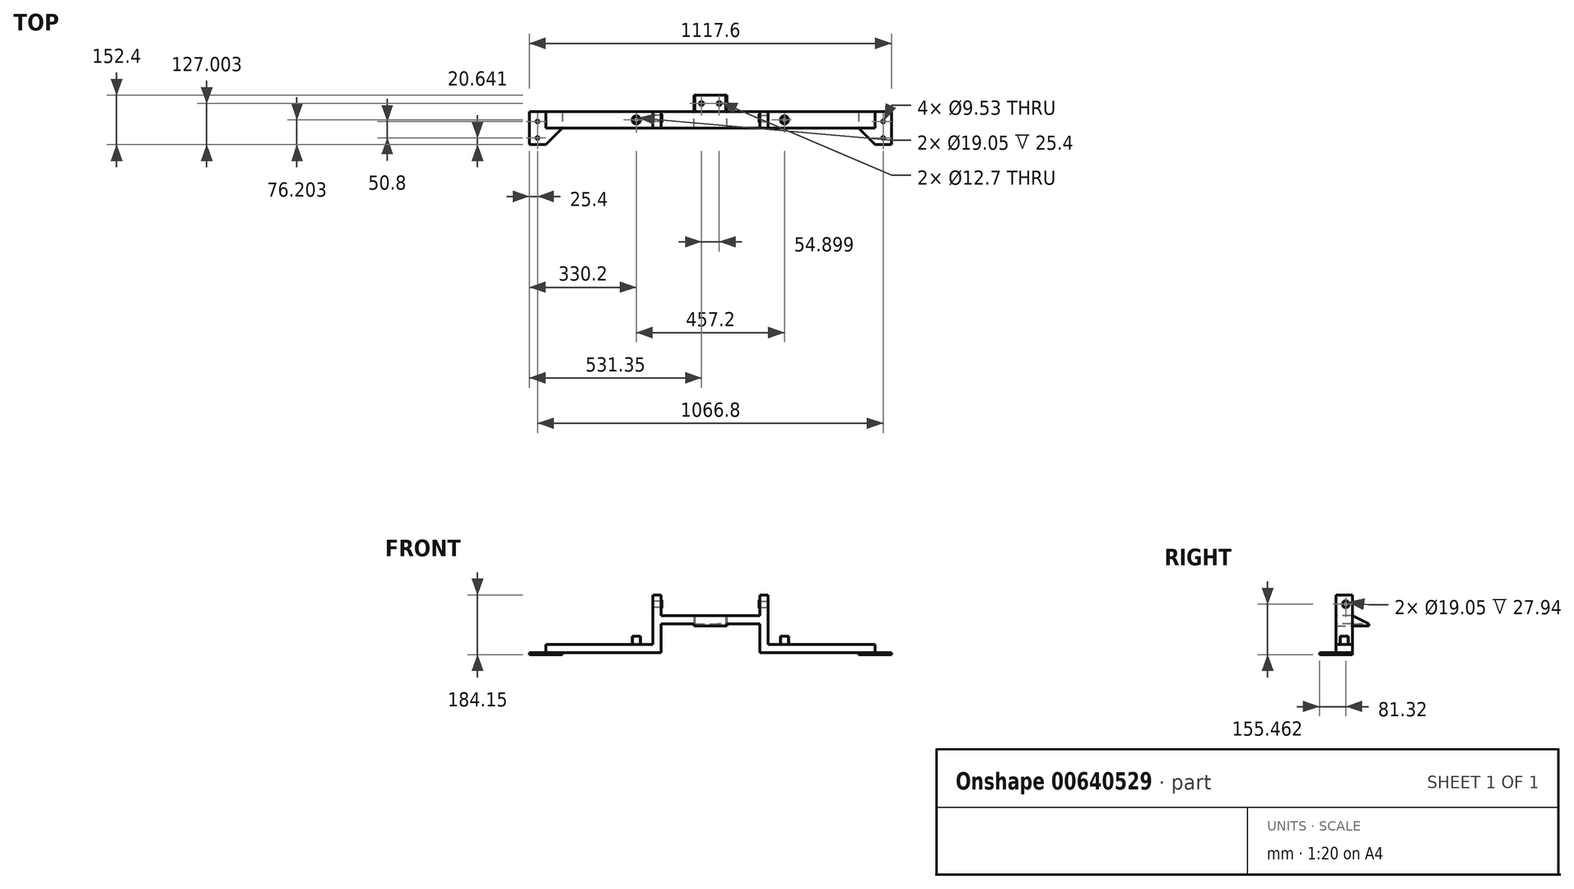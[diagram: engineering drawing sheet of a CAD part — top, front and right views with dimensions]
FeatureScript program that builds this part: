
annotation { "Feature Type Name" : "Feature", "Feature Type Description" : "" }
export const myFeature = defineFeature(function(context is Context, id is Id, definition is map)
    precondition{}
    {
        {
            var Q0;
            Q0=qCreatedBy(makeId("Top.planeOp"),FACE);
            var sketch = newSketch(context, id + "F0", { "sketchPlane" : qUnion([Q0])});
            skLineSegment(sketch, "E0.bottom", {"start": v(0, 37.2) * mm, "end": v(355.6, 37.2) * mm});
            skLineSegment(sketch, "E0.top", {"start": v(0, -13.6) * mm, "end": v(355.6, -13.6) * mm});
            skLineSegment(sketch, "E0.left", {"start": v(0, 37.2) * mm, "end": v(0, -13.6) * mm});
            skLineSegment(sketch, "E0.right", {"start": v(355.6, 37.2) * mm, "end": v(355.6, -13.6) * mm});
            skSolve(sketch);
        }
        {
            var Q0;
            Q0=makeQuery(id+"F0.imprint","IMPRINT",FACE,{"disambiguationData":[TD([[makeQuery(id+"F0.imprint","IMPRINT",EDGE,{"derivedFrom":sQuery(id+"F0.wireOp",EDGE,"E0.bottom")}),-1.0]])]});
            extrude(context, id + "F1", {"entities" : qUnion([Q0]), "depth" : 25.4 * mm, "offsetDistance" : 25.4 * mm});
        }
        {
            var Q0;
            Q0=qCreatedBy(makeId("Top.planeOp"),FACE);
            var sketch = newSketch(context, id + "F2", { "sketchPlane" : qUnion([Q0])});
            skLineSegment(sketch, "E1.0", {"start": v(0, 37.2) * mm, "end": v(355.6, 37.2) * mm});
            skLineSegment(sketch, "E2.0", {"start": v(0, -13.6) * mm, "end": v(355.6, -13.6) * mm});
            skLineSegment(sketch, "E3", {"start": v(304.8, -13.6) * mm, "end": v(355.6, -64.4) * mm});
            skLineSegment(sketch, "E4", {"start": v(355.6, -64.4) * mm, "end": v(406.4, -64.4) * mm});
            skLineSegment(sketch, "E5", {"start": v(406.4, -64.4) * mm, "end": v(406.4, 37.2) * mm});
            skLineSegment(sketch, "E6", {"start": v(406.4, 37.2) * mm, "end": v(304.8, 37.2) * mm});
            skLineSegment(sketch, "E7", {"start": v(304.8, 37.2) * mm, "end": v(304.8, -13.6) * mm});
            skSolve(sketch);
        }
        {
            var Q0;
            Q0 = qSketchRegion(id + "F2", true);
            extrude(context, id + "F3", {"entities" : qUnion([Q0]), "operationType" : NewBodyOperationType.ADD, "oppositeDirection" : true, "depth" : 6.35 * mm, "offsetDistance" : 25.4 * mm});
        }
        {
            var Q0;
            Q0=makeQuery(id+"F3.opExtrude","CAP_FACE",FACE,{"disambiguationData":[OSD([sQuery(id+"F2.wireOp",EDGE,"E3"),sQuery(id+"F2.wireOp",EDGE,"E4"),sQuery(id+"F2.wireOp",EDGE,"E5"),sQuery(id+"F2.wireOp",EDGE,"E6"),sQuery(id+"F2.wireOp",EDGE,"E7")])],"isStart":true});
            var sketch = newSketch(context, id + "F4", { "sketchPlane" : qUnion([Q0])});
            skCircle(sketch, "E8", {"center": v(381, -43.77) * mm, "radius": 4.76 * mm});
            skCircle(sketch, "E9", {"center": v(381, 7.03) * mm, "radius": 4.76 * mm});
            skSolve(sketch);
        }
        {
            var Q0;
            Q0 = qSketchRegion(id + "F4", true);
            extrude(context, id + "F5", {"entities" : qUnion([Q0]), "operationType" : NewBodyOperationType.REMOVE, "oppositeDirection" : true, "depth" : 25.4 * mm, "offsetDistance" : 25.4 * mm});
        }
        {
            var Q0;
            Q0=makeQuery(id+"F1.opExtrude","CAP_FACE",FACE,{"disambiguationData":[OSD([sQuery(id+"F0.wireOp",EDGE,"E0.bottom"),sQuery(id+"F0.wireOp",EDGE,"E0.top"),sQuery(id+"F0.wireOp",EDGE,"E0.left"),sQuery(id+"F0.wireOp",EDGE,"E0.right")])],"isStart":false});
            var sketch = newSketch(context, id + "F6", { "sketchPlane" : qUnion([Q0])});
            skCircle(sketch, "E10", {"center": v(76.2, 11.8) * mm, "radius": 12.7 * mm});
            skCircle(sketch, "E11", {"center": v(76.2, 11.8) * mm, "radius": 9.53 * mm});
            skSolve(sketch);
        }
        {
            var Q0;
            Q0=makeQuery(id+"F6.imprint","IMPRINT",FACE,{"disambiguationData":[TD([[makeQuery(id+"F6.imprint","IMPRINT",EDGE,{"derivedFrom":sQuery(id+"F6.wireOp",EDGE,"E10")}),1.0]])]});
            var Q1;
            Q1=sQuery(id+"F6.wireOp",EDGE,"E10");
            var Q2;
            Q2=sQuery(id+"F6.wireOp",EDGE,"E11");
            extrude(context, id + "F7", {"entities" : qUnion([Q0]), "operationType" : NewBodyOperationType.ADD, "surfaceEntities" : qUnion([Q1, Q2]), "depth" : 25.4 * mm, "offsetDistance" : 25.4 * mm});
        }
        {
            var Q0;
            Q0=makeQuery(id+"F1.opExtrude","CAP_FACE",FACE,{"disambiguationData":[OSD([sQuery(id+"F0.wireOp",EDGE,"E0.bottom"),sQuery(id+"F0.wireOp",EDGE,"E0.top"),sQuery(id+"F0.wireOp",EDGE,"E0.left"),sQuery(id+"F0.wireOp",EDGE,"E0.right")])],"isStart":false});
            var sketch = newSketch(context, id + "F8", { "sketchPlane" : qUnion([Q0])});
            skLineSegment(sketch, "E12.bottom", {"start": v(0, 37.2) * mm, "end": v(25.4, 37.2) * mm});
            skLineSegment(sketch, "E12.top", {"start": v(0, -13.6) * mm, "end": v(25.4, -13.6) * mm});
            skLineSegment(sketch, "E12.left", {"start": v(0, 37.2) * mm, "end": v(0, -13.6) * mm});
            skLineSegment(sketch, "E12.right", {"start": v(25.4, 37.2) * mm, "end": v(25.4, -13.6) * mm});
            skSolve(sketch);
        }
        {
            var Q0;
            Q0 = qSketchRegion(id + "F8", true);
            extrude(context, id + "F9", {"entities" : qUnion([Q0]), "operationType" : NewBodyOperationType.ADD, "depth" : 152.4 * mm, "offsetDistance" : 25.4 * mm});
        }
        {
            var Q0;
            Q0=makeQuery(id+"F9.boolean.opBoolean","MERGE",FACE,{"derivedFrom":[makeQuery(id+"F1.opExtrude","SWEPT_FACE",FACE,{"disambiguationData":[OSD([sQuery(id+"F0.wireOp",EDGE,"E0.left")])]}),makeQuery(id+"F9.opExtrude","SWEPT_FACE",FACE,{"disambiguationData":[OSD([sQuery(id+"F8.wireOp",EDGE,"E12.left")])]})]});
            var sketch = newSketch(context, id + "F10", { "sketchPlane" : qUnion([Q0])});
            skLineSegment(sketch, "E13.bottom", {"start": v(-37.2, 114.3) * mm, "end": v(13.6, 114.3) * mm});
            skLineSegment(sketch, "E13.top", {"start": v(-37.2, 88.9) * mm, "end": v(13.6, 88.9) * mm});
            skLineSegment(sketch, "E13.left", {"start": v(-37.2, 114.3) * mm, "end": v(-37.2, 88.9) * mm});
            skLineSegment(sketch, "E13.right", {"start": v(13.6, 114.3) * mm, "end": v(13.6, 88.9) * mm});
            skSolve(sketch);
        }
        {
            var Q0;
            Q0 = qSketchRegion(id + "F10", true);
            extrude(context, id + "F11", {"entities" : qUnion([Q0]), "operationType" : NewBodyOperationType.ADD, "depth" : 152.4 * mm, "offsetDistance" : 25.4 * mm});
        }
        {
            var Q0;
            {var subQ1=sQuery(id+"F8.wireOp",EDGE,"E12.left");Q0=makeQuery(id+"F11.boolean.opBoolean","SPLIT",FACE,{"disambiguationData":[TD([makeQuery(id+"F11.opExtrude","SWEPT_FACE",FACE,{"disambiguationData":[OSD([sQuery(id+"F10.wireOp",EDGE,"E13.bottom")])]})])],"derivedFrom":makeQuery(id+"F9.boolean.opBoolean","MERGE",FACE,{"derivedFrom":[makeQuery(id+"F1.opExtrude","SWEPT_FACE",FACE,{"disambiguationData":[OSD([sQuery(id+"F0.wireOp",EDGE,"E0.left")])]}),makeQuery(id+"F9.opExtrude","SWEPT_FACE",FACE,{"disambiguationData":[OSD([subQ1])]})]})});}
            var sketch = newSketch(context, id + "F12", { "sketchPlane" : qUnion([Q0])});
            skCircle(sketch, "E14", {"center": v(-16.9, 149.11) * mm, "radius": 12.7 * mm});
            skCircle(sketch, "E15", {"center": v(-16.9, 149.11) * mm, "radius": 9.53 * mm});
            skSolve(sketch);
        }
        {
            var Q0;
            Q0 = qSketchRegion(id + "F12", true);
            extrude(context, id + "F13", {"entities" : qUnion([Q0]), "operationType" : NewBodyOperationType.ADD, "depth" : 2.54 * mm, "offsetDistance" : 25.4 * mm});
        }
        {
            var Q0;
            {var subQ1=sQuery(id+"F8.wireOp",EDGE,"E12.left");Q0=makeQuery(id+"F13.boolean.opBoolean","SPLIT",FACE,{"disambiguationData":[TD([makeQuery(id+"F13.opExtrude","SWEPT_FACE",FACE,{"disambiguationData":[OSD([sQuery(id+"F12.wireOp",EDGE,"E15")])]})])],"derivedFrom":makeQuery(id+"F11.boolean.opBoolean","SPLIT",FACE,{"disambiguationData":[TD([makeQuery(id+"F11.opExtrude","SWEPT_FACE",FACE,{"disambiguationData":[OSD([sQuery(id+"F10.wireOp",EDGE,"E13.bottom")])]})])],"derivedFrom":makeQuery(id+"F9.boolean.opBoolean","MERGE",FACE,{"derivedFrom":[makeQuery(id+"F1.opExtrude","SWEPT_FACE",FACE,{"disambiguationData":[OSD([sQuery(id+"F0.wireOp",EDGE,"E0.left")])]}),makeQuery(id+"F9.opExtrude","SWEPT_FACE",FACE,{"disambiguationData":[OSD([subQ1])]})]})})});}
            var sketch = newSketch(context, id + "F14", { "sketchPlane" : qUnion([Q0])});
            skCircle(sketch, "E16", {"center": v(-16.9, 149.11) * mm, "radius": 9.53 * mm});
            skSolve(sketch);
        }
        {
            var Q0;
            Q0 = qSketchRegion(id + "F14", true);
            extrude(context, id + "F15", {"entities" : qUnion([Q0]), "operationType" : NewBodyOperationType.REMOVE, "oppositeDirection" : true, "depth" : 25.4 * mm, "offsetDistance" : 25.4 * mm});
        }
        {
            var Q0;
            Q0=makeQuery(id+"F11.opExtrude","SWEPT_FACE",FACE,{"disambiguationData":[OSD([sQuery(id+"F10.wireOp",EDGE,"E13.top")])]});
            var sketch = newSketch(context, id + "F16", { "sketchPlane" : qUnion([Q0])});
            skLineSegment(sketch, "E17.bottom", {"start": v(-101.6, 13.6) * mm, "end": v(-152.4, 13.6) * mm});
            skLineSegment(sketch, "E17.top", {"start": v(-101.6, -88) * mm, "end": v(-152.4, -88) * mm});
            skLineSegment(sketch, "E17.left", {"start": v(-101.6, 13.6) * mm, "end": v(-101.6, -88) * mm});
            skLineSegment(sketch, "E17.right", {"start": v(-152.4, 13.6) * mm, "end": v(-152.4, -88) * mm});
            skSolve(sketch);
        }
        {
            var Q0;
            Q0 = qSketchRegion(id + "F16", true);
            extrude(context, id + "F17", {"entities" : qUnion([Q0]), "operationType" : NewBodyOperationType.ADD, "depth" : 6.35 * mm, "offsetDistance" : 25.4 * mm});
        }
        {
            var Q0;
            Q0=makeQuery(id+"F17.opExtrude","CAP_FACE",FACE,{"disambiguationData":[OSD([sQuery(id+"F16.wireOp",EDGE,"E17.bottom"),sQuery(id+"F16.wireOp",EDGE,"E17.top"),sQuery(id+"F16.wireOp",EDGE,"E17.left"),sQuery(id+"F16.wireOp",EDGE,"E17.right")])],"isStart":true});
            var sketch = newSketch(context, id + "F18", { "sketchPlane" : qUnion([Q0])});
            skCircle(sketch, "E18", {"center": v(-124.95, 62.6) * mm, "radius": 6.35 * mm});
            skPoint(sketch, "E18.centerSnap0", {"position": v(-101.6, 62.6) * mm});
            skSolve(sketch);
        }
        {
            var Q0;
            Q0 = qSketchRegion(id + "F18", true);
            extrude(context, id + "F19", {"entities" : qUnion([Q0]), "operationType" : NewBodyOperationType.REMOVE, "oppositeDirection" : true, "depth" : 25.4 * mm, "offsetDistance" : 25.4 * mm});
        }
        {
            var Q0;
            Q0=makeQuery(id+"F17.opExtrude","SWEPT_FACE",FACE,{"disambiguationData":[OSD([sQuery(id+"F16.wireOp",EDGE,"E17.left")])]});
            var sketch = newSketch(context, id + "F20", { "sketchPlane" : qUnion([Q0])});
            skLineSegment(sketch, "E19", {"start": v(88, 88.9) * mm, "end": v(37.2, 114.3) * mm});
            skLineSegment(sketch, "E20", {"start": v(37.2, 114.3) * mm, "end": v(37.2, 82.55) * mm});
            skLineSegment(sketch, "E21", {"start": v(37.2, 82.55) * mm, "end": v(88, 82.55) * mm});
            skLineSegment(sketch, "E22", {"start": v(88, 82.55) * mm, "end": v(37.2, 82.55) * mm});
            skSolve(sketch);
        }
        {
            var Q0;
            {var subQ0=sQuery(id+"F20.wireOp",EDGE,"E19");Q0=makeQuery(id+"F20.imprint","IMPRINT",FACE,{"disambiguationData":[TD([[makeQuery(id+"F20.imprint","IMPRINT",EDGE,{"derivedFrom":subQ0}),1.0]])]});}
            var Q1;
            {var subQ6=sQuery(id+"F20.wireOp",EDGE,"E22");Q1=makeQuery(id+"F20.imprint","IMPRINT",FACE,{"disambiguationData":[TD([[makeQuery(id+"F20.imprint","IMPRINT",EDGE,{"derivedFrom":subQ6}),1.0]])]});}
            extrude(context, id + "F21", {"entities" : qUnion([Q0, Q1]), "operationType" : NewBodyOperationType.ADD, "oppositeDirection" : true, "depth" : 3.17 * mm, "offsetDistance" : 25.4 * mm});
        }
        {
            var Q0;
            Q0=makeQuery(id+"F1.opExtrude","SWEPT_BODY",BODY,{"disambiguationData":[OSD([sQuery(id+"F0.wireOp",EDGE,"E0.bottom"),sQuery(id+"F0.wireOp",EDGE,"E0.top"),sQuery(id+"F0.wireOp",EDGE,"E0.left"),sQuery(id+"F0.wireOp",EDGE,"E0.right")])]});
            var Q1;
            Q1=makeQuery(id+"F17.boolean.opBoolean","MERGE",FACE,{"derivedFrom":[makeQuery(id+"F11.opExtrude","CAP_FACE",FACE,{"disambiguationData":[OSD([sQuery(id+"F10.wireOp",EDGE,"E13.bottom"),sQuery(id+"F10.wireOp",EDGE,"E13.top"),sQuery(id+"F10.wireOp",EDGE,"E13.left"),sQuery(id+"F10.wireOp",EDGE,"E13.right")])],"isStart":false}),makeQuery(id+"F17.opExtrude","SWEPT_FACE",FACE,{"disambiguationData":[OSD([sQuery(id+"F16.wireOp",EDGE,"E17.right")])]})]});
            mirror(context, id + "F22", {"operationType" : NewBodyOperationType.ADD, "entities" : qUnion([Q0]), "mirrorPlane" : qUnion([Q1])});
        }
    });
